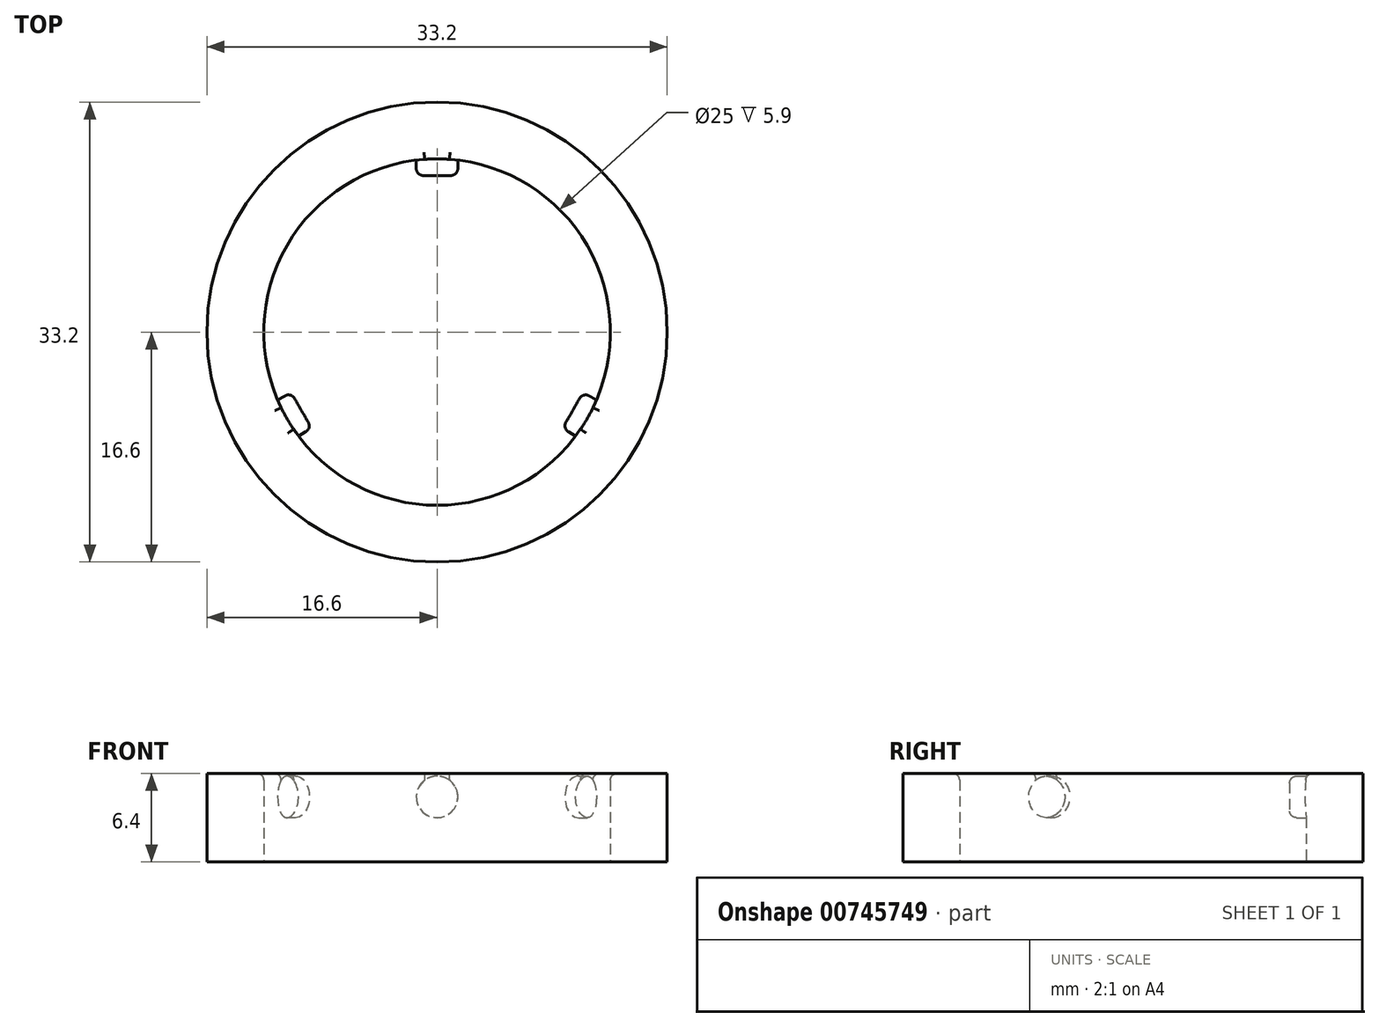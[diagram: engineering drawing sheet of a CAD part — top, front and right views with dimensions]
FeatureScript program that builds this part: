
annotation { "Feature Type Name" : "Feature", "Feature Type Description" : "" }
export const myFeature = defineFeature(function(context is Context, id is Id, definition is map)
    precondition{}
    {
        {
            var Q0;
            Q0=qCreatedBy(makeId("Top.planeOp"),FACE);
            var sketch = newSketch(context, id + "F0", { "sketchPlane" : qUnion([Q0])});
            skCircle(sketch, "E0", {"center": v(0, 0) * mm, "radius": 12.5 * mm});
            skCircle(sketch, "E1", {"center": v(0, 0) * mm, "radius": 16.6 * mm});
            skLineSegment(sketch, "E2", {"start": v(0, 12.5) * mm, "end": v(0, 16.6) * mm, "construction": true});
            skLineSegment(sketch, "E3", {"start": v(-1.12, 12.5) * mm, "end": v(1.28, 12.5) * mm, "construction": true});
            skLineSegment(sketch, "E4", {"start": v(0, 12.5) * mm, "end": v(0, 0) * mm, "construction": true});
            skLineSegment(sketch, "E5", {"start": v(0, 0) * mm, "end": v(10.83, -6.25) * mm, "construction": true});
            skLineSegment(sketch, "E6", {"start": v(0, 0) * mm, "end": v(-10.83, -6.25) * mm, "construction": true});
            skLineSegment(sketch, "E7", {"start": v(11.56, -4.98) * mm, "end": v(10.16, -7.4) * mm, "construction": true});
            skLineSegment(sketch, "E8", {"start": v(-11.13, -5.73) * mm, "end": v(-10.5, -6.83) * mm, "construction": true});
            skSolve(sketch);
        }
        {
            var Q0;
            Q0=sQuery(id+"F0.wireOp",EDGE,"E3");
            var Q1;
            Q1=makeQuery(id+"F0.imprint","IMPRINT",FACE,{"disambiguationData":[TD([[makeQuery(id+"F0.imprint","IMPRINT",EDGE,{"derivedFrom":sQuery(id+"F0.wireOp",EDGE,"E0")}),1.0]])]});
            var Q2;
            Q2 = qBodyType(qCreatedBy(id + "F5" ,EDGE), BodyType.WIRE);
            cPlane(context, id + "F1", {"entities" : qUnion([Q0, Q1, Q2]), "cplaneType" : CPlaneType.LINE_ANGLE, "offset" : 25 * mm, "angle" : 90 * degree, "width" : 150 * mm, "height" : 150 * mm});
        }
        {
            var Q0;
            Q0=sQuery(id+"F0.wireOp",EDGE,"E7");
            var Q1;
            Q1=makeQuery(id+"F0.imprint","IMPRINT",FACE,{"disambiguationData":[TD([[makeQuery(id+"F0.imprint","IMPRINT",EDGE,{"derivedFrom":sQuery(id+"F0.wireOp",EDGE,"E0")}),-1.0]])]});
            cPlane(context, id + "F2", {"entities" : qUnion([Q0, Q1]), "cplaneType" : CPlaneType.LINE_ANGLE, "offset" : 25 * mm, "angle" : 90 * degree, "width" : 150 * mm, "height" : 150 * mm});
        }
        {
            var Q0;
            Q0=sQuery(id+"F0.wireOp",EDGE,"E8");
            var Q1;
            Q1=makeQuery(id+"F0.imprint","IMPRINT",FACE,{"disambiguationData":[TD([[makeQuery(id+"F0.imprint","IMPRINT",EDGE,{"derivedFrom":sQuery(id+"F0.wireOp",EDGE,"E0")}),1.0]])]});
            cPlane(context, id + "F3", {"entities" : qUnion([Q0, Q1]), "cplaneType" : CPlaneType.LINE_ANGLE, "offset" : 25 * mm, "angle" : 90 * degree, "width" : 150 * mm, "height" : 150 * mm});
        }
        {
            var Q0;
            Q0=makeQuery(id+"F0.imprint","IMPRINT",FACE,{"disambiguationData":[TD([[makeQuery(id+"F0.imprint","IMPRINT",EDGE,{"derivedFrom":sQuery(id+"F0.wireOp",EDGE,"E0")}),-1.0]])]});
            extrude(context, id + "F4", {"entities" : qUnion([Q0]), "depth" : 3.4 * mm, "offsetDistance" : 25 * mm});
        }
        {
            var Q0;
            Q0=qCreatedBy(id+"F1.planeOp",FACE);
            var sketch = newSketch(context, id + "F5", { "sketchPlane" : qUnion([Q0])});
            skLineSegment(sketch, "E9", {"start": v(0, 0) * mm, "end": v(0, 3.4) * mm, "construction": true});
            skPoint(sketch, "E10", {"position": v(0, 1.7) * mm});
            skCircle(sketch, "E11", {"center": v(0, 1.7) * mm, "radius": 1.5 * mm});
            skSolve(sketch);
        }
        {
            var Q0;
            Q0=qCreatedBy(id+"F2.planeOp",FACE);
            var sketch = newSketch(context, id + "F6", { "sketchPlane" : qUnion([Q0])});
            skLineSegment(sketch, "E12", {"start": v(0, 0) * mm, "end": v(0, 3.4) * mm, "construction": true});
            skPoint(sketch, "E13", {"position": v(0, 1.7) * mm});
            skCircle(sketch, "E14", {"center": v(0, 1.7) * mm, "radius": 1.5 * mm});
            skSolve(sketch);
        }
        {
            var Q0;
            Q0=qCreatedBy(id+"F3.planeOp",FACE);
            var sketch = newSketch(context, id + "F7", { "sketchPlane" : qUnion([Q0])});
            skLineSegment(sketch, "E15", {"start": v(0, 0) * mm, "end": v(0, 3.4) * mm, "construction": true});
            skPoint(sketch, "E16", {"position": v(0, 1.7) * mm});
            skCircle(sketch, "E17", {"center": v(0, 1.7) * mm, "radius": 1.5 * mm});
            skSolve(sketch);
        }
        {
            var Q0;
            Q0 = qSketchRegion(id + "F7", true);
            extrude(context, id + "F8", {"entities" : qUnion([Q0]), "operationType" : NewBodyOperationType.ADD, "depth" : 1.2 * mm, "offsetDistance" : 25 * mm});
        }
        {
            var Q0;
            Q0 = qSketchRegion(id + "F6", true);
            var Q1;
            Q1=sQuery(id+"F6.wireOp",EDGE,"E14");
            extrude(context, id + "F9", {"entities" : qUnion([Q0]), "operationType" : NewBodyOperationType.ADD, "surfaceEntities" : qUnion([Q1]), "oppositeDirection" : true, "depth" : 1.2 * mm, "offsetDistance" : 25 * mm});
        }
        {
            var Q0;
            Q0=makeQuery(id+"F5.imprint","IMPRINT",FACE,{"disambiguationData":[TD([[makeQuery(id+"F5.imprint","IMPRINT",EDGE,{"derivedFrom":sQuery(id+"F5.wireOp",EDGE,"E11")}),1.0]])]});
            var Q1;
            Q1=sQuery(id+"F5.wireOp",EDGE,"E11");
            extrude(context, id + "F10", {"entities" : qUnion([Q0]), "operationType" : NewBodyOperationType.ADD, "surfaceOperationType" : NewSurfaceOperationType.ADD, "surfaceEntities" : qUnion([Q1]), "oppositeDirection" : true, "depth" : 1.2 * mm, "offsetDistance" : 25 * mm});
        }
        {
            var Q0;
            Q0=makeQuery(id+"F9.opExtrude","CAP_EDGE",EDGE,{"disambiguationData":[OSD([sQuery(id+"F6.wireOp",EDGE,"E14")])],"isStart":false});
            var Q1;
            Q1=makeQuery(id+"F8.opExtrude","CAP_EDGE",EDGE,{"disambiguationData":[OSD([sQuery(id+"F7.wireOp",EDGE,"E17")])],"isStart":false});
            var Q2;
            Q2=makeQuery(id+"F10.opExtrude","CAP_EDGE",EDGE,{"disambiguationData":[OSD([sQuery(id+"F5.wireOp",EDGE,"E11")])],"isStart":false});
            fillet(context, id + "F11", {"entities" : qUnion([Q0, Q1, Q2]), "radius" : 0.5 * mm, "tangentPropagation" : true, "allowEdgeOverflow" : false});
        }
        {
            var Q0;
            Q0=makeQuery(id+"F0.imprint","IMPRINT",FACE,{"disambiguationData":[TD([[makeQuery(id+"F0.imprint","IMPRINT",EDGE,{"derivedFrom":sQuery(id+"F0.wireOp",EDGE,"E0")}),-1.0]])]});
            extrude(context, id + "F12", {"entities" : qUnion([Q0]), "operationType" : NewBodyOperationType.ADD, "oppositeDirection" : true, "depth" : 3 * mm, "offsetDistance" : 25 * mm});
        }
        {
            var Q0;
            Q0=makeQuery(id+"F4.opExtrude","CAP_EDGE",EDGE,{"disambiguationData":[OSD([sQuery(id+"F0.wireOp",EDGE,"E0")])],"isStart":false});
            fillet(context, id + "F13", {"entities" : qUnion([Q0]), "radius" : 0.5 * mm, "tangentPropagation" : true, "allowEdgeOverflow" : false});
        }
    });
